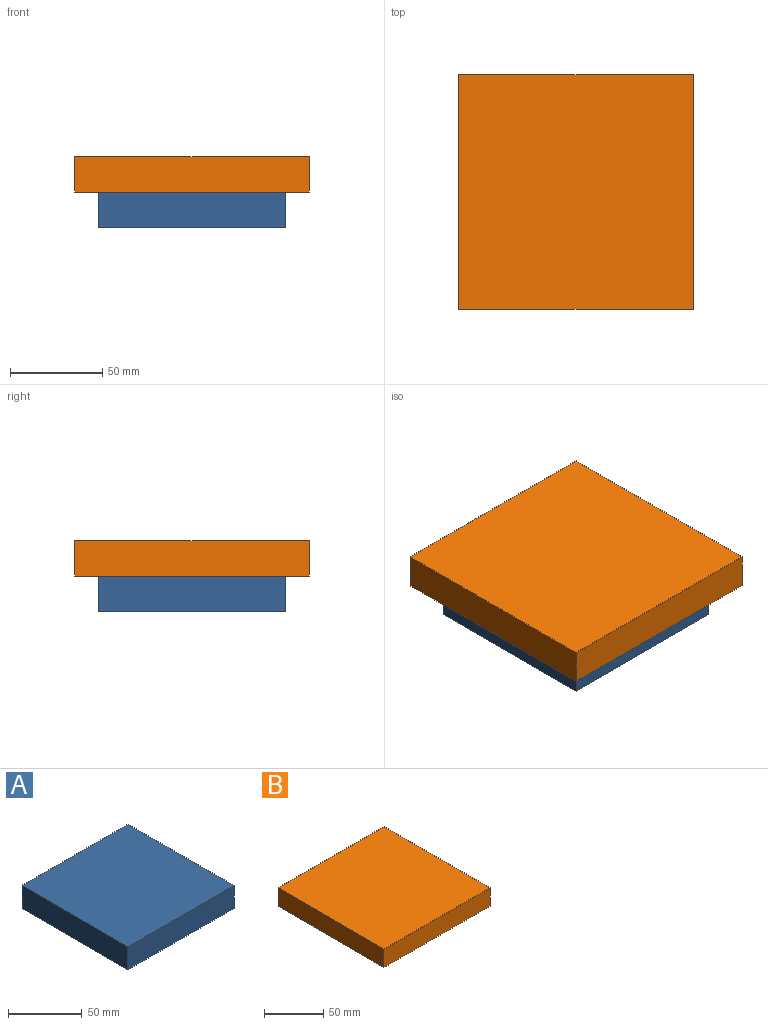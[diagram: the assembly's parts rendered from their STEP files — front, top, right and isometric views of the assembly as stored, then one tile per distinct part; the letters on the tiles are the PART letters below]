
ASSEMBLY  parts=2 mates=1
PART A: 6 faces, bbox 101.6x101.6x19.1 mm
  f0: plane 101.6x19.05mm, normal (0,-1,0), area 1935.5mm2, adj f1,f3,f4,f5
  f1: plane 101.6x19.05mm, normal (1,0,0), area 1935.5mm2, adj f0,f2,f4,f5
  f2: plane 101.6x19.05mm, normal (0,1,0), area 1935.5mm2, adj f1,f3,f4,f5
  f3: plane 101.6x19.05mm, normal (-1,0,0), area 1935.5mm2, adj f0,f2,f4,f5
  f4: plane 101.6x101.6mm, normal (0,0,1), area 10322.6mm2, adj f0,f1,f2,f3
  f5: plane 101.6x101.6mm, normal (0,0,-1), area 10322.6mm2, adj f0,f1,f2,f3
PART B: 6 faces, bbox 127x127x19.1 mm
  f0: plane 127x19.05mm, normal (0,-1,0), area 2419.3mm2, adj f1,f3,f4,f5
  f1: plane 127x19.05mm, normal (1,0,0), area 2419.3mm2, adj f0,f2,f4,f5
  f2: plane 127x19.05mm, normal (0,1,0), area 2419.3mm2, adj f1,f3,f4,f5
  f3: plane 127x19.05mm, normal (-1,0,0), area 2419.3mm2, adj f0,f2,f4,f5
  f4: plane 127x127mm, normal (0,0,1), area 16129mm2, adj f0,f1,f2,f3
  f5: plane 127x127mm, normal (0,0,-1), area 16129mm2, adj f0,f1,f2,f3
PLACE A at identity fixed
PLACE B t=(0,0,19.05)mm
MATE fastened A.f4 <-> B.f5  axis (0,0,1) through (50.8,-50.8,19.05)mm
